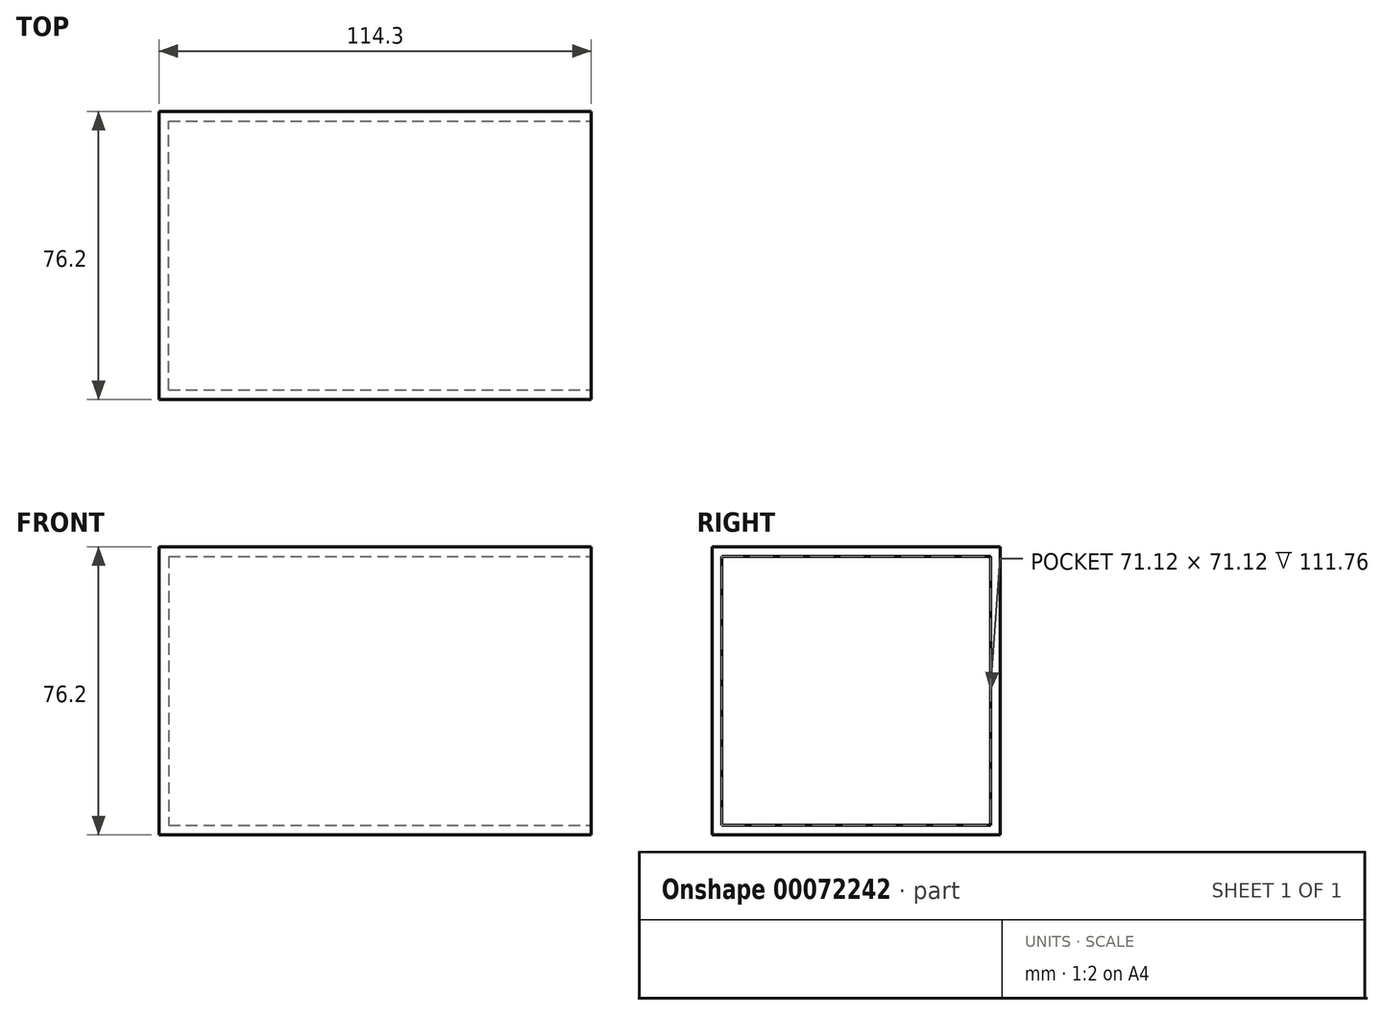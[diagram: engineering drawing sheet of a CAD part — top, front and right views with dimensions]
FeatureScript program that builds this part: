
annotation { "Feature Type Name" : "Feature", "Feature Type Description" : "" }
export const myFeature = defineFeature(function(context is Context, id is Id, definition is map)
    precondition{}
    {
        {
            var Q0;
            Q0=qCreatedBy(makeId("Front.planeOp"),FACE);
            var sketch = newSketch(context, id + "F0", { "sketchPlane" : qUnion([Q0])});
            skLineSegment(sketch, "E0.bottom", {"start": v(-55.32, 12.53) * mm, "end": v(58.98, 12.53) * mm});
            skLineSegment(sketch, "E0.top", {"start": v(-55.32, -63.67) * mm, "end": v(58.98, -63.67) * mm});
            skLineSegment(sketch, "E0.left", {"start": v(-55.32, 12.53) * mm, "end": v(-55.32, -63.67) * mm});
            skLineSegment(sketch, "E0.right", {"start": v(58.98, 12.53) * mm, "end": v(58.98, -63.67) * mm});
            skSolve(sketch);
        }
        {
            var Q0;
            Q0=makeQuery(id+"F0.imprint","IMPRINT",FACE,{"disambiguationData":[TD([[makeQuery(id+"F0.imprint","IMPRINT",EDGE,{"derivedFrom":sQuery(id+"F0.wireOp",EDGE,"E0.bottom")}),-1.0]])]});
            extrude(context, id + "F1", {"entities" : qUnion([Q0]), "depth" : 76.2 * mm});
        }
        {
            var Q0;
            Q0=makeQuery(id+"F1.opExtrude","SWEPT_FACE",FACE,{"disambiguationData":[OSD([sQuery(id+"F0.wireOp",EDGE,"E0.right")])]});
            shell(context, id + "F2", {"entities" : qUnion([Q0]), "thickness" : 2.54 * mm});
        }
    });
